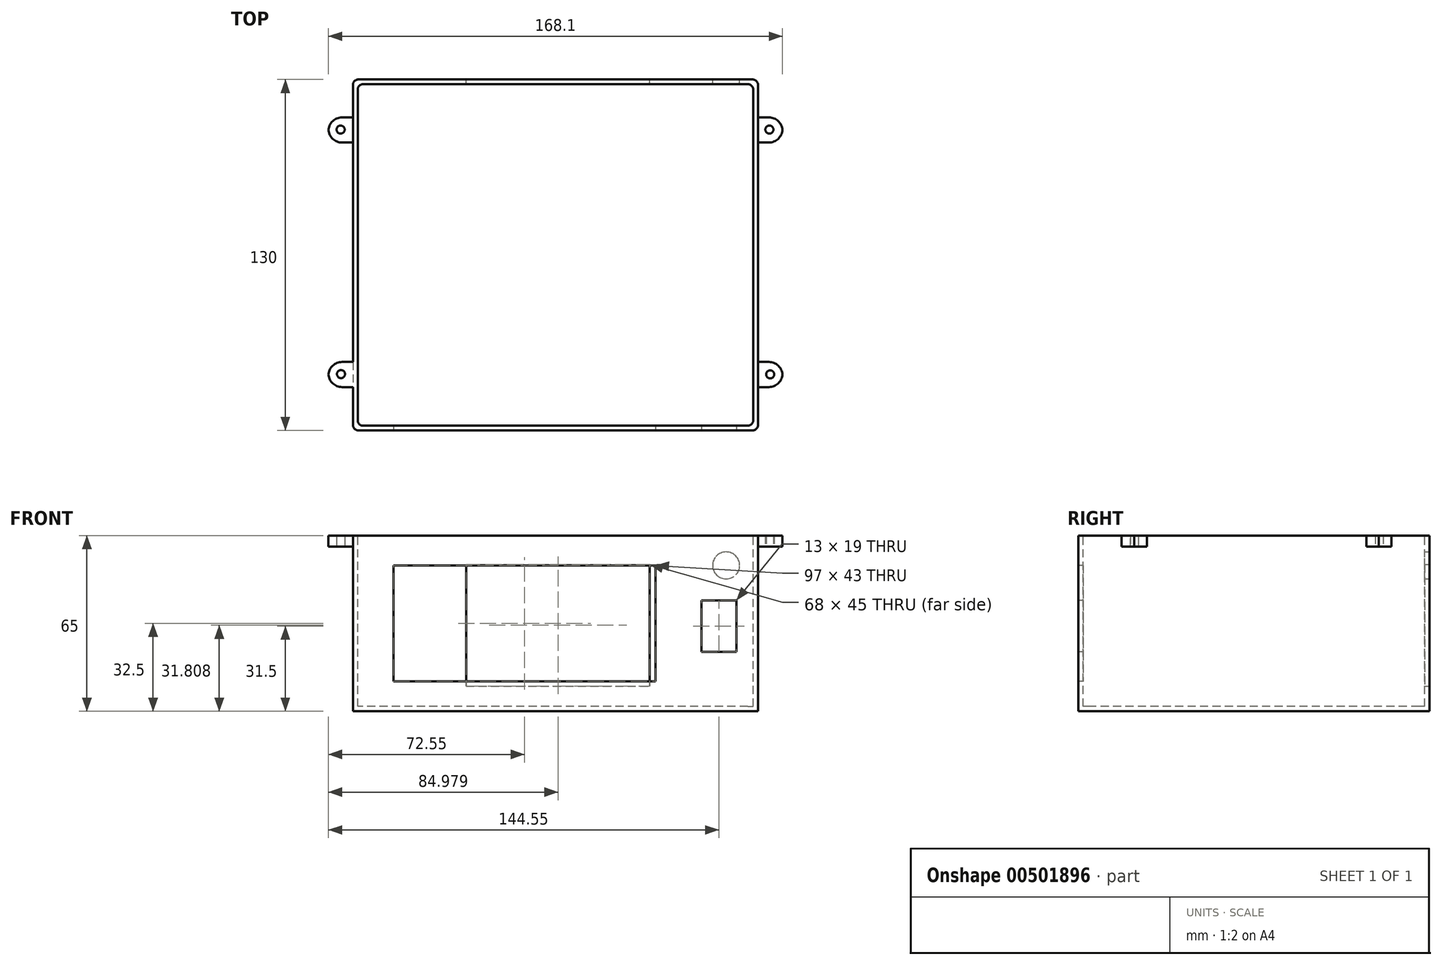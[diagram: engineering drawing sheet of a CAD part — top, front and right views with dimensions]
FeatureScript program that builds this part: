
annotation { "Feature Type Name" : "Feature", "Feature Type Description" : "" }
export const myFeature = defineFeature(function(context is Context, id is Id, definition is map)
    precondition{}
    {
        {
            var Q0;
            Q0=qCreatedBy(makeId("Front.planeOp"),FACE);
            var sketch = newSketch(context, id + "F0", { "sketchPlane" : qUnion([Q0])});
            skLineSegment(sketch, "E0.bottom", {"start": v(0, 0) * mm, "end": v(-150, 0) * mm});
            skLineSegment(sketch, "E0.top", {"start": v(0, 65) * mm, "end": v(-150, 65) * mm});
            skLineSegment(sketch, "E0.left", {"start": v(0, 0) * mm, "end": v(0, 65) * mm});
            skLineSegment(sketch, "E0.right", {"start": v(-150, 0) * mm, "end": v(-150, 65) * mm});
            skSolve(sketch);
        }
        {
            var Q0;
            Q0 = qSketchRegion(id + "F0", true);
            extrude(context, id + "F1", {"entities" : qUnion([Q0]), "oppositeDirection" : true, "depth" : 130 * mm});
        }
        {
            var Q0;
            Q0=makeQuery(id+"F1.opExtrude","SWEPT_FACE",FACE,{"disambiguationData":[OSD([sQuery(id+"F0.wireOp",EDGE,"E0.top")])]});
            shell(context, id + "F2", {"entities" : qUnion([Q0]), "thickness" : 1.75 * mm});
        }
        {
            var Q0;
            Q0=makeQuery(id+"F1.opExtrude","CAP_EDGE",EDGE,{"disambiguationData":[OSD([sQuery(id+"F0.wireOp",EDGE,"E0.left")])],"isStart":true});
            var Q1;
            Q1=makeQuery(id+"F1.opExtrude","CAP_EDGE",EDGE,{"disambiguationData":[OSD([sQuery(id+"F0.wireOp",EDGE,"E0.right")])],"isStart":true});
            fillet(context, id + "F3", {"entities" : qUnion([Q0, Q1]), "radius" : 2 * mm, "tangentPropagation" : true, "allowEdgeOverflow" : false});
        }
        {
            var Q0;
            Q0=makeQuery(id+"F1.opExtrude","CAP_FACE",FACE,{"disambiguationData":[OSD([sQuery(id+"F0.wireOp",EDGE,"E0.bottom"),sQuery(id+"F0.wireOp",EDGE,"E0.top"),sQuery(id+"F0.wireOp",EDGE,"E0.left"),sQuery(id+"F0.wireOp",EDGE,"E0.right")])],"isStart":false});
            var sketch = newSketch(context, id + "F4", { "sketchPlane" : qUnion([Q0])});
            skLineSegment(sketch, "E1.bottom", {"start": v(108.07, 9.3) * mm, "end": v(40.07, 9.3) * mm});
            skLineSegment(sketch, "E1.top", {"start": v(108.07, 54.3) * mm, "end": v(40.07, 54.3) * mm});
            skLineSegment(sketch, "E1.left", {"start": v(108.07, 9.3) * mm, "end": v(108.07, 54.3) * mm});
            skLineSegment(sketch, "E1.right", {"start": v(40.07, 9.3) * mm, "end": v(40.07, 54.3) * mm});
            skPoint(sketch, "E1.middle", {"position": v(74.07, 31.8) * mm});
            skSolve(sketch);
        }
        {
            var Q0;
            Q0 = qSketchRegion(id + "F4", true);
            extrude(context, id + "F5", {"entities" : qUnion([Q0]), "operationType" : NewBodyOperationType.REMOVE, "oppositeDirection" : true, "depth" : 2 * mm});
        }
        {
            var Q0;
            Q0=makeQuery(id+"F1.opExtrude","SWEPT_FACE",FACE,{"disambiguationData":[OSD([sQuery(id+"F0.wireOp",EDGE,"E0.top")])]});
            var sketch = newSketch(context, id + "F6", { "sketchPlane" : qUnion([Q0])});
            skLineSegment(sketch, "E2.bottom", {"start": v(-150, 16.05) * mm, "end": v(-159.06, 16.05) * mm});
            skLineSegment(sketch, "E2.top", {"start": v(-150, 25.35) * mm, "end": v(-159.06, 25.35) * mm});
            skLineSegment(sketch, "E2.left", {"start": v(-150, 16.05) * mm, "end": v(-150, 25.35) * mm});
            skLineSegment(sketch, "E2.right", {"start": v(-159.06, 16.05) * mm, "end": v(-159.06, 25.35) * mm});
            skLineSegment(sketch, "E3", {"start": v(-75, -4.08) * mm, "end": v(-75, 135.08) * mm, "construction": true});
            skPoint(sketch, "E3.startSnap0", {"position": v(-75, 0) * mm});
            skLineSegment(sketch, "E4.MirrorCS", {"start": v(0, 16.05) * mm, "end": v(9.06, 16.05) * mm});
            skLineSegment(sketch, "E5.MirrorCS", {"start": v(0, 16.05) * mm, "end": v(0, 25.35) * mm});
            skLineSegment(sketch, "E6.MirrorCS", {"start": v(9.06, 16.05) * mm, "end": v(9.06, 25.35) * mm});
            skLineSegment(sketch, "E7.MirrorCS", {"start": v(0, 25.35) * mm, "end": v(9.06, 25.35) * mm});
            skLineSegment(sketch, "E8", {"start": v(0, 66) * mm, "end": v(-184.06, 66) * mm, "construction": true});
            skLineSegment(sketch, "E9.MirrorCS", {"start": v(-150, 106.65) * mm, "end": v(-159.06, 106.65) * mm});
            skLineSegment(sketch, "E10.MirrorCS", {"start": v(-150, 115.95) * mm, "end": v(-159.06, 115.95) * mm});
            skLineSegment(sketch, "E11.MirrorCS", {"start": v(-150, 115.95) * mm, "end": v(-150, 106.65) * mm});
            skLineSegment(sketch, "E12.MirrorCS", {"start": v(-159.06, 115.95) * mm, "end": v(-159.06, 106.65) * mm});
            skLineSegment(sketch, "E13.MirrorCS", {"start": v(0, 106.65) * mm, "end": v(9.06, 106.65) * mm});
            skLineSegment(sketch, "E14.MirrorCS", {"start": v(9.06, 115.95) * mm, "end": v(9.06, 106.65) * mm});
            skLineSegment(sketch, "E15.MirrorCS", {"start": v(0, 115.95) * mm, "end": v(9.06, 115.95) * mm});
            skLineSegment(sketch, "E16.MirrorCS", {"start": v(0, 115.95) * mm, "end": v(0, 106.65) * mm});
            skSolve(sketch);
        }
        {
            var Q0;
            Q0=makeQuery(id+"F6.imprint","IMPRINT",FACE,{"disambiguationData":[TD([[makeQuery(id+"F6.imprint","IMPRINT",EDGE,{"derivedFrom":sQuery(id+"F6.wireOp",EDGE,"E2.bottom")}),-1.0]])]});
            extrude(context, id + "F7", {"entities" : qUnion([Q0]), "operationType" : NewBodyOperationType.ADD, "oppositeDirection" : true, "depth" : 4 * mm});
        }
        {
            var Q0;
            Q0=makeQuery(id+"F7.boolean.opBoolean","MERGE",FACE,{"derivedFrom":[makeQuery(id+"F1.opExtrude","SWEPT_FACE",FACE,{"disambiguationData":[OSD([sQuery(id+"F0.wireOp",EDGE,"E0.top")])]}),makeQuery(id+"F7.opExtrude","CAP_FACE",FACE,{"disambiguationData":[OSD([sQuery(id+"F6.wireOp",EDGE,"E2.bottom"),sQuery(id+"F6.wireOp",EDGE,"E2.top"),sQuery(id+"F6.wireOp",EDGE,"E2.left"),sQuery(id+"F6.wireOp",EDGE,"E2.right")])],"isStart":true})]});
            var sketch = newSketch(context, id + "F8", { "sketchPlane" : qUnion([Q0])});
            skPoint(sketch, "E17", {"position": v(-154.42, 20.85) * mm});
            skSolve(sketch);
        }
        {
            var Q0;
            Q0=sQuery(id+"F8.wireOp",VERTEX,"E17");
            var Q1;
            Q1=makeQuery(id+"F1.opExtrude","SWEPT_BODY",BODY,{"disambiguationData":[OSD([sQuery(id+"F0.wireOp",EDGE,"E0.bottom"),sQuery(id+"F0.wireOp",EDGE,"E0.top"),sQuery(id+"F0.wireOp",EDGE,"E0.left"),sQuery(id+"F0.wireOp",EDGE,"E0.right")])]});
            hole(context, id + "F9", {"style" : HoleStyle.C_SINK, "endStyle" : HoleEndStyle.THROUGH, "holeDiameter" : 3 * mm, "cSinkDiameter" : 3 * mm, "cSinkAngle" : 45 * degree, "isTappedThrough" : true, "tappedDepth" : 12 * mm, "tapClearance" : 3, "locations" : qUnion([Q0]), "scope" : qUnion([Q1])});
        }
        {
            var Q0;
            Q0=makeQuery(id+"F6.imprint","IMPRINT",FACE,{"disambiguationData":[TD([[makeQuery(id+"F6.imprint","IMPRINT",EDGE,{"derivedFrom":sQuery(id+"F6.wireOp",EDGE,"E9.MirrorCS")}),-1.0]])]});
            var Q1;
            Q1=makeQuery(id+"F6.imprint","IMPRINT",FACE,{"disambiguationData":[TD([[makeQuery(id+"F6.imprint","IMPRINT",EDGE,{"derivedFrom":sQuery(id+"F6.wireOp",EDGE,"E13.MirrorCS")}),1.0]])]});
            var Q2;
            Q2=makeQuery(id+"F6.imprint","IMPRINT",FACE,{"disambiguationData":[TD([[makeQuery(id+"F6.imprint","IMPRINT",EDGE,{"derivedFrom":sQuery(id+"F6.wireOp",EDGE,"E4.MirrorCS")}),1.0]])]});
            extrude(context, id + "F10", {"entities" : qUnion([Q0, Q1, Q2]), "oppositeDirection" : true, "depth" : 4 * mm});
        }
        {
            var Q0;
            Q0=makeQuery(id+"F2.opShell","OFFSET_FACE",FACE,{"disambiguationData":[OSD([sQuery(id+"F0.wireOp",EDGE,"E0.bottom")])]});
            var sketch = newSketch(context, id + "F11", { "sketchPlane" : qUnion([Q0])});
            skPoint(sketch, "E18", {"position": v(-154.56, 111.44) * mm});
            skPoint(sketch, "E19", {"position": v(4.22, 111.44) * mm});
            skPoint(sketch, "E20", {"position": v(4.51, 20.75) * mm});
            skSolve(sketch);
        }
        {
            var Q0;
            Q0=sQuery(id+"F11.wireOp",VERTEX,"E18");
            var Q1;
            Q1=sQuery(id+"F11.wireOp",VERTEX,"E19");
            var Q2;
            Q2=sQuery(id+"F11.wireOp",VERTEX,"E20");
            var Q3;
            Q3=makeQuery(id+"F10.opExtrude","SWEPT_BODY",BODY,{"disambiguationData":[OSD([sQuery(id+"F6.wireOp",EDGE,"E9.MirrorCS"),sQuery(id+"F6.wireOp",EDGE,"E10.MirrorCS"),sQuery(id+"F6.wireOp",EDGE,"E11.MirrorCS"),sQuery(id+"F6.wireOp",EDGE,"E12.MirrorCS")])]});
            var Q4;
            Q4=makeQuery(id+"F10.opExtrude","SWEPT_BODY",BODY,{"disambiguationData":[OSD([sQuery(id+"F6.wireOp",EDGE,"E13.MirrorCS"),sQuery(id+"F6.wireOp",EDGE,"E14.MirrorCS"),sQuery(id+"F6.wireOp",EDGE,"E15.MirrorCS"),sQuery(id+"F6.wireOp",EDGE,"E16.MirrorCS")])]});
            var Q5;
            Q5=makeQuery(id+"F10.opExtrude","SWEPT_BODY",BODY,{"disambiguationData":[OSD([sQuery(id+"F6.wireOp",EDGE,"E4.MirrorCS"),sQuery(id+"F6.wireOp",EDGE,"E5.MirrorCS"),sQuery(id+"F6.wireOp",EDGE,"E6.MirrorCS"),sQuery(id+"F6.wireOp",EDGE,"E7.MirrorCS")])]});
            hole(context, id + "F12", {"style" : HoleStyle.C_SINK, "endStyle" : HoleEndStyle.THROUGH, "oppositeDirection" : true, "holeDiameter" : 3 * mm, "cSinkDiameter" : 3 * mm, "cSinkAngle" : 45 * degree, "isTappedThrough" : true, "tappedDepth" : 12 * mm, "tapClearance" : 3, "locations" : qUnion([Q0, Q1, Q2]), "scope" : qUnion([Q3, Q4, Q5])});
        }
        {
            var Q0;
            Q0=makeQuery(id+"F1.opExtrude","CAP_FACE",FACE,{"disambiguationData":[OSD([sQuery(id+"F0.wireOp",EDGE,"E0.bottom"),sQuery(id+"F0.wireOp",EDGE,"E0.top"),sQuery(id+"F0.wireOp",EDGE,"E0.left"),sQuery(id+"F0.wireOp",EDGE,"E0.right")])],"isStart":true});
            var sketch = newSketch(context, id + "F13", { "sketchPlane" : qUnion([Q0])});
            skLineSegment(sketch, "E21.bottom", {"start": v(-21, 41) * mm, "end": v(-8, 41) * mm});
            skLineSegment(sketch, "E21.top", {"start": v(-21, 22) * mm, "end": v(-8, 22) * mm});
            skLineSegment(sketch, "E21.left", {"start": v(-21, 41) * mm, "end": v(-21, 22) * mm});
            skLineSegment(sketch, "E21.right", {"start": v(-8, 41) * mm, "end": v(-8, 22) * mm});
            skSolve(sketch);
        }
        {
            var Q0;
            Q0=makeQuery(id+"F13.imprint","IMPRINT",FACE,{"disambiguationData":[TD([[makeQuery(id+"F13.imprint","IMPRINT",EDGE,{"derivedFrom":sQuery(id+"F13.wireOp",EDGE,"E21.bottom")}),-1.0]])]});
            extrude(context, id + "F14", {"entities" : qUnion([Q0]), "operationType" : NewBodyOperationType.REMOVE, "oppositeDirection" : true, "depth" : 2 * mm});
        }
        {
            var Q0;
            Q0=makeQuery(id+"F1.opExtrude","CAP_FACE",FACE,{"disambiguationData":[OSD([sQuery(id+"F0.wireOp",EDGE,"E0.bottom"),sQuery(id+"F0.wireOp",EDGE,"E0.top"),sQuery(id+"F0.wireOp",EDGE,"E0.left"),sQuery(id+"F0.wireOp",EDGE,"E0.right")])],"isStart":false});
            var sketch = newSketch(context, id + "F15", { "sketchPlane" : qUnion([Q0])});
            skPoint(sketch, "E22", {"position": v(11.8, 53.98) * mm});
            skSolve(sketch);
        }
        {
            var Q0;
            Q0=sQuery(id+"F15.wireOp",VERTEX,"E22");
            var Q1;
            Q1=makeQuery(id+"F1.opExtrude","SWEPT_BODY",BODY,{"disambiguationData":[OSD([sQuery(id+"F0.wireOp",EDGE,"E0.bottom"),sQuery(id+"F0.wireOp",EDGE,"E0.top"),sQuery(id+"F0.wireOp",EDGE,"E0.left"),sQuery(id+"F0.wireOp",EDGE,"E0.right")])]});
            hole(context, id + "F16", {"style" : HoleStyle.C_SINK, "endStyle" : HoleEndStyle.BLIND, "holeDiameter" : 10 * mm, "cSinkDiameter" : 10 * mm, "cSinkAngle" : 45 * degree, "holeDepth" : 20 * mm, "isTappedThrough" : true, "tappedDepth" : 12 * mm, "tapClearance" : 3, "locations" : qUnion([Q0]), "scope" : qUnion([Q1])});
        }
        {
            var Q0;
            Q0=makeQuery(id+"F1.opExtrude","CAP_EDGE",EDGE,{"disambiguationData":[OSD([sQuery(id+"F0.wireOp",EDGE,"E0.left")])],"isStart":false});
            var Q1;
            Q1=makeQuery(id+"F1.opExtrude","CAP_EDGE",EDGE,{"disambiguationData":[OSD([sQuery(id+"F0.wireOp",EDGE,"E0.right")])],"isStart":false});
            var Q2;
            {var subQ0=sQuery(id+"F0.wireOp",EDGE,"E0.right");Q2=makeQuery(id+"F2.opShell","OFFSET_EDGE",EDGE,{"disambiguationData":[OSD([subQ0]),TDD([makeQuery(id+"F1.opExtrude","CAP_EDGE",EDGE,{"disambiguationData":[OSD([subQ0])],"isStart":true})])]});}
            var Q3;
            {var subQ0=sQuery(id+"F0.wireOp",EDGE,"E0.left");Q3=makeQuery(id+"F2.opShell","OFFSET_EDGE",EDGE,{"disambiguationData":[OSD([subQ0]),TDD([makeQuery(id+"F1.opExtrude","CAP_EDGE",EDGE,{"disambiguationData":[OSD([subQ0])],"isStart":true})])]});}
            var Q4;
            {var subQ0=sQuery(id+"F0.wireOp",EDGE,"E0.left");Q4=makeQuery(id+"F2.opShell","OFFSET_EDGE",EDGE,{"disambiguationData":[OSD([subQ0]),TDD([makeQuery(id+"F1.opExtrude","CAP_EDGE",EDGE,{"disambiguationData":[OSD([subQ0])],"isStart":false})])]});}
            var Q5;
            {var subQ0=sQuery(id+"F0.wireOp",EDGE,"E0.right");Q5=makeQuery(id+"F2.opShell","OFFSET_EDGE",EDGE,{"disambiguationData":[OSD([subQ0]),TDD([makeQuery(id+"F1.opExtrude","CAP_EDGE",EDGE,{"disambiguationData":[OSD([subQ0])],"isStart":false})])]});}
            fillet(context, id + "F17", {"entities" : qUnion([Q0, Q1, Q2, Q3, Q4, Q5]), "radius" : 2 * mm, "tangentPropagation" : true, "allowEdgeOverflow" : false});
        }
        {
            var Q0;
            Q0=makeQuery(id+"F10.opExtrude","SWEPT_EDGE",EDGE,{"disambiguationData":[OSD([sQuery(id+"F6.wireOp",EDGE,"E14.MirrorCS"),sQuery(id+"F6.wireOp",EDGE,"E15.MirrorCS")])]});
            var Q1;
            Q1=makeQuery(id+"F10.opExtrude","SWEPT_EDGE",EDGE,{"disambiguationData":[OSD([sQuery(id+"F6.wireOp",EDGE,"E13.MirrorCS"),sQuery(id+"F6.wireOp",EDGE,"E14.MirrorCS")])]});
            var Q2;
            Q2=makeQuery(id+"F10.opExtrude","SWEPT_EDGE",EDGE,{"disambiguationData":[OSD([sQuery(id+"F6.wireOp",EDGE,"E4.MirrorCS"),sQuery(id+"F6.wireOp",EDGE,"E6.MirrorCS")])]});
            var Q3;
            Q3=makeQuery(id+"F10.opExtrude","SWEPT_EDGE",EDGE,{"disambiguationData":[OSD([sQuery(id+"F6.wireOp",EDGE,"E6.MirrorCS"),sQuery(id+"F6.wireOp",EDGE,"E7.MirrorCS")])]});
            var Q4;
            Q4=makeQuery(id+"F10.opExtrude","SWEPT_EDGE",EDGE,{"disambiguationData":[OSD([sQuery(id+"F6.wireOp",EDGE,"E9.MirrorCS"),sQuery(id+"F6.wireOp",EDGE,"E12.MirrorCS")])]});
            var Q5;
            Q5=makeQuery(id+"F10.opExtrude","SWEPT_EDGE",EDGE,{"disambiguationData":[OSD([sQuery(id+"F6.wireOp",EDGE,"E10.MirrorCS"),sQuery(id+"F6.wireOp",EDGE,"E12.MirrorCS")])]});
            var Q6;
            Q6=makeQuery(id+"F7.opExtrude","SWEPT_EDGE",EDGE,{"disambiguationData":[OSD([sQuery(id+"F6.wireOp",EDGE,"E2.top"),sQuery(id+"F6.wireOp",EDGE,"E2.right")])]});
            var Q7;
            Q7=makeQuery(id+"F7.opExtrude","SWEPT_EDGE",EDGE,{"disambiguationData":[OSD([sQuery(id+"F6.wireOp",EDGE,"E2.bottom"),sQuery(id+"F6.wireOp",EDGE,"E2.right")])]});
            fillet(context, id + "F18", {"entities" : qUnion([Q0, Q1, Q2, Q3, Q4, Q5, Q6, Q7]), "radius" : 5 * mm, "tangentPropagation" : true, "allowEdgeOverflow" : false});
        }
        {
            var Q0;
            Q0=makeQuery(id+"F1.opExtrude","CAP_FACE",FACE,{"disambiguationData":[OSD([sQuery(id+"F0.wireOp",EDGE,"E0.bottom"),sQuery(id+"F0.wireOp",EDGE,"E0.top"),sQuery(id+"F0.wireOp",EDGE,"E0.left"),sQuery(id+"F0.wireOp",EDGE,"E0.right")])],"isStart":true});
            var sketch = newSketch(context, id + "F19", { "sketchPlane" : qUnion([Q0])});
            skLineSegment(sketch, "E23.bottom", {"start": v(-135, 54) * mm, "end": v(-38, 54) * mm});
            skLineSegment(sketch, "E23.top", {"start": v(-135, 11) * mm, "end": v(-38, 11) * mm});
            skLineSegment(sketch, "E23.left", {"start": v(-135, 54) * mm, "end": v(-135, 11) * mm});
            skLineSegment(sketch, "E23.right", {"start": v(-38, 54) * mm, "end": v(-38, 11) * mm});
            skSolve(sketch);
        }
        {
            var Q0;
            Q0 = qSketchRegion(id + "F19", true);
            extrude(context, id + "F20", {"entities" : qUnion([Q0]), "operationType" : NewBodyOperationType.REMOVE, "oppositeDirection" : true, "depth" : 2 * mm});
        }
    });
